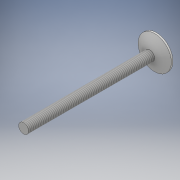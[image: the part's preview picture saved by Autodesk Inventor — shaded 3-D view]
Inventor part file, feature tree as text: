
AUTODESK INVENTOR PART (.ipt)
format: ipt  version: 2018 (Build 220112000, 112)  size: 134,656 bytes
history: native  units: mm
features: sketch x2, revolve x1, extrude x1, thread x1
ambient origin geometry x8: Origin, YZ Plane, XZ Plane, XY Plane, X Axis, Y Axis, Z Axis, Center Point
bodies: Solid1 (feature_tree)
feature tree (5):
  revolve  "Revolution1"  [1 undecoded]
  extrude  "Extrusion1"  Depth=10.0mm
  thread  "Thread1"  [1 undecoded]
  sketch  "Sketch1"  dims[d0=1.5mm d1=40.0mm]
  sketch  "Sketch2"  dims[d2=5.0mm d3=38.0mm d4=90.0deg d5=3.4mm d6=3.4mm d8=1.0mm d9=40.0mm d11=360.0deg d13=0.5mm d14=0.0mm d15=0.5mm d16=10.0mm d17=0.0mm]
note: 2 required parameter values undecoded (feature->parameter linkage not recoverable at this tier; creation-order binding heuristic only, values carry confidence <= 0.55)